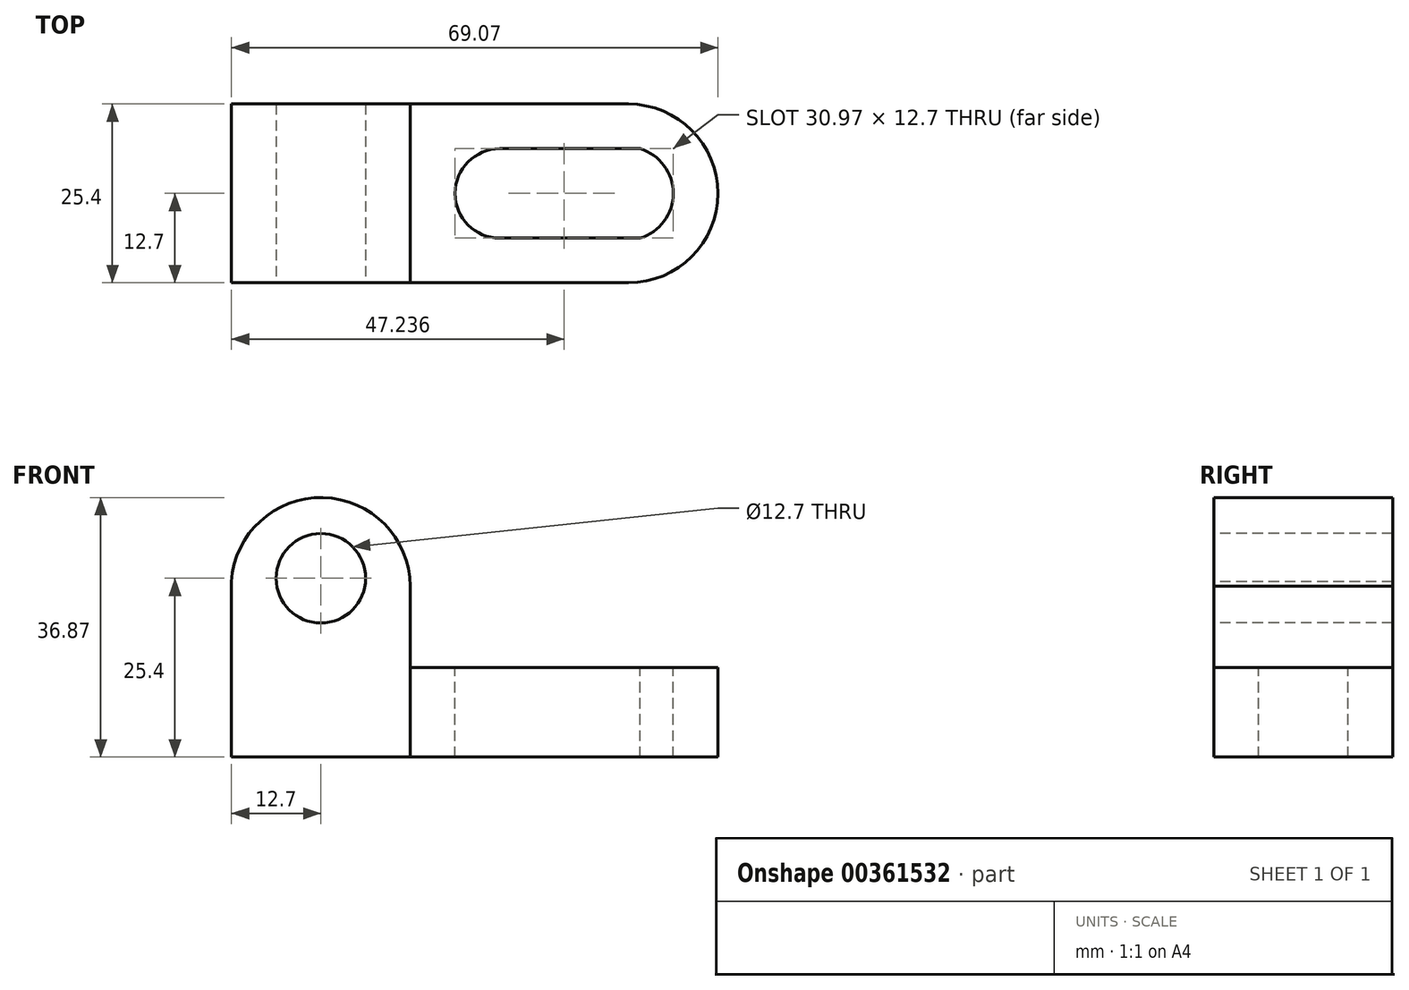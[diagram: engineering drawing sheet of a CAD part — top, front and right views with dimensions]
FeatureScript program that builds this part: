
annotation { "Feature Type Name" : "Feature", "Feature Type Description" : "" }
export const myFeature = defineFeature(function(context is Context, id is Id, definition is map)
    precondition{}
    {
        {
            var Q0;
            Q0=qCreatedBy(makeId("Top.planeOp"),FACE);
            var sketch = newSketch(context, id + "F0", { "sketchPlane" : qUnion([Q0])});
            skLineSegment(sketch, "E0", {"start": v(0, 25.4) * mm, "end": v(0, 0) * mm});
            skLineSegment(sketch, "E1", {"start": v(0, 25.4) * mm, "end": v(44.45, 25.4) * mm});
            skLineSegment(sketch, "E2", {"start": v(44.45, 25.4) * mm, "end": v(44.45, 0) * mm});
            skLineSegment(sketch, "E3", {"start": v(44.45, 0) * mm, "end": v(0, 0) * mm});
            skSolve(sketch);
        }
        {
            var Q0;
            Q0 = qSketchRegion(id + "F0", true);
            extrude(context, id + "F1", {"entities" : qUnion([Q0]), "depth" : 12.7 * mm});
        }
        {
            var Q0;
            Q0=makeQuery(id+"F1.opExtrude","CAP_FACE",FACE,{"disambiguationData":[OSD([sQuery(id+"F0.wireOp",EDGE,"E0"),sQuery(id+"F0.wireOp",EDGE,"E1"),sQuery(id+"F0.wireOp",EDGE,"E2"),sQuery(id+"F0.wireOp",EDGE,"E3")])],"isStart":false});
            var sketch = newSketch(context, id + "F2", { "sketchPlane" : qUnion([Q0])});
            skArc(sketch, "E4", {"start": v(30.97, 0) * mm, "mid": v(43.67, 12.7) * mm, "end": v(30.97, 25.4) * mm});
            skSolve(sketch);
        }
        {
            var Q0;
            {var subQ0=sQuery(id+"F2.wireOp",EDGE,"E4");Q0=makeQuery(id+"F2.imprint","IMPRINT",FACE,{"disambiguationData":[TD([[makeQuery(id+"F2.imprint","IMPRINT",EDGE,{"derivedFrom":subQ0}),-1.0]])]});}
            extrude(context, id + "F3", {"entities" : qUnion([Q0]), "operationType" : NewBodyOperationType.REMOVE, "oppositeDirection" : true, "depth" : 12.7 * mm});
        }
        {
            var Q0;
            Q0=makeQuery(id+"F1.opExtrude","CAP_FACE",FACE,{"disambiguationData":[OSD([sQuery(id+"F0.wireOp",EDGE,"E0"),sQuery(id+"F0.wireOp",EDGE,"E1"),sQuery(id+"F0.wireOp",EDGE,"E2"),sQuery(id+"F0.wireOp",EDGE,"E3")])],"isStart":false});
            var sketch = newSketch(context, id + "F4", { "sketchPlane" : qUnion([Q0])});
            skLineSegment(sketch, "E5", {"start": v(12.7, 19.05) * mm, "end": v(32.64, 19.05) * mm});
            skArc(sketch, "E6", {"start": v(12.7, 19.05) * mm, "mid": v(6.35, 12.7) * mm, "end": v(12.7, 6.35) * mm});
            skLineSegment(sketch, "E7", {"start": v(12.7, 6.35) * mm, "end": v(32.64, 6.35) * mm});
            skArc(sketch, "E8", {"start": v(32.64, 6.35) * mm, "mid": v(37.32, 12.7) * mm, "end": v(32.64, 19.05) * mm});
            skSolve(sketch);
        }
        {
            var Q0;
            Q0 = qSketchRegion(id + "F4", true);
            extrude(context, id + "F5", {"entities" : qUnion([Q0]), "operationType" : NewBodyOperationType.ADD, "depth" : 25.4 * mm});
        }
        {
            var Q0;
            Q0=makeQuery(id+"F5.opExtrude","CAP_FACE",FACE,{"disambiguationData":[OSD([sQuery(id+"F4.wireOp",EDGE,"E5"),sQuery(id+"F4.wireOp",EDGE,"E6"),sQuery(id+"F4.wireOp",EDGE,"E7"),sQuery(id+"F4.wireOp",EDGE,"E8")])],"isStart":false});
            var sketch = newSketch(context, id + "F6", { "sketchPlane" : qUnion([Q0])});
            skSolve(sketch);
        }
        {
            var Q0;
            Q0=makeQuery(id+"F6.imprint","IMPRINT",FACE,{"disambiguationData":[TD([[makeQuery(id+"F6.imprint","IMPRINT",EDGE,{"derivedFrom":makeQuery(id+"F5.opExtrude","CAP_EDGE",EDGE,{"disambiguationData":[OSD([sQuery(id+"F4.wireOp",EDGE,"E5")])],"isStart":false})}),-1.0]])]});
            extrude(context, id + "F7", {"entities" : qUnion([Q0]), "operationType" : NewBodyOperationType.REMOVE, "oppositeDirection" : true, "depth" : 38.1 * mm});
        }
        {
            var Q0;
            Q0=makeQuery(id+"F1.opExtrude","SWEPT_FACE",FACE,{"disambiguationData":[OSD([sQuery(id+"F0.wireOp",EDGE,"E3")])]});
            var sketch = newSketch(context, id + "F8", { "sketchPlane" : qUnion([Q0])});
            skLineSegment(sketch, "E9", {"start": v(0, 0) * mm, "end": v(0, 38.1) * mm});
            skLineSegment(sketch, "E10", {"start": v(0, 38.1) * mm, "end": v(-25.4, 38.1) * mm});
            skLineSegment(sketch, "E11", {"start": v(-25.4, 38.1) * mm, "end": v(-25.4, 0) * mm});
            skLineSegment(sketch, "E12", {"start": v(-25.4, 0) * mm, "end": v(0, 0) * mm});
            skCircle(sketch, "E13", {"center": v(-12.7, 25.4) * mm, "radius": 6.35 * mm});
            skArc(sketch, "E14", {"start": v(0, 25.4) * mm, "mid": v(-12.7, 37.56) * mm, "end": v(-25.4, 25.4) * mm});
            skSolve(sketch);
        }
        {
            var Q0;
            {var subQ0=sQuery(id+"F8.wireOp",EDGE,"E10");Q0=makeQuery(id+"F8.imprint","IMPRINT",FACE,{"disambiguationData":[TD([[makeQuery(id+"F8.imprint","IMPRINT",EDGE,{"derivedFrom":subQ0}),1.0]])]});}
            var Q1;
            {var subQ0=sQuery(id+"F8.wireOp",EDGE,"E12");Q1=makeQuery(id+"F8.imprint","IMPRINT",FACE,{"disambiguationData":[TD([[makeQuery(id+"F8.imprint","IMPRINT",EDGE,{"derivedFrom":subQ0}),1.0]])]});}
            extrude(context, id + "F9", {"entities" : qUnion([Q0, Q1]), "oppositeDirection" : true, "depth" : 25.4 * mm});
        }
        {
            var Q0;
            Q0=makeQuery(id+"F9.opExtrude","CAP_FACE",FACE,{"disambiguationData":[OSD([sQuery(id+"F8.wireOp",EDGE,"E9"),sQuery(id+"F8.wireOp",EDGE,"E10"),sQuery(id+"F8.wireOp",EDGE,"E11"),sQuery(id+"F8.wireOp",EDGE,"E12"),sQuery(id+"F8.wireOp",EDGE,"E13")])],"isStart":true});
            var sketch = newSketch(context, id + "F10", { "sketchPlane" : qUnion([Q0])});
            skArc(sketch, "E15", {"start": v(0, 24.3) * mm, "mid": v(-12.4, 36.86) * mm, "end": v(-25.4, 24.92) * mm});
            skSolve(sketch);
        }
        {
            var Q0;
            Q0 = qSketchRegion(id + "F10", true);
            var Q1;
            {var subQ0=sQuery(id+"F10.wireOp",EDGE,"E15");Q1=makeQuery(id+"F10.imprint","IMPRINT",FACE,{"disambiguationData":[TD([[makeQuery(id+"F10.imprint","IMPRINT",EDGE,{"derivedFrom":subQ0}),-1.0]])]});}
            extrude(context, id + "F11", {"entities" : qUnion([Q0, Q1]), "operationType" : NewBodyOperationType.REMOVE, "oppositeDirection" : true, "depth" : 25.4 * mm});
        }
    });
